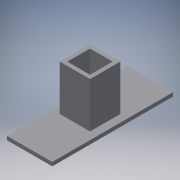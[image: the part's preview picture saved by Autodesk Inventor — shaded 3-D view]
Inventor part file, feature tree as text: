
AUTODESK INVENTOR PART (.ipt)
format: ipt  version: 2016 (Build 200138000, 138)  size: 104,960 bytes
history: native  units: in
note: dims shown in document units (in); Inventor stores cm internally (conversion verified against a paired STEP export)
features: extrude x2, sketch x2
ambient origin geometry x8: Origin, YZ Plane, XZ Plane, XY Plane, X Axis, Y Axis, Z Axis, Center Point
bodies: Solid1 (feature_tree)
feature tree (4):
  extrude  "Extrusion1"  Depth=4.0in
  extrude  "Extrusion3"  Depth=1.0in
  sketch  "Sketch1"  dims[d0=1.5in d1=4.0in]
  sketch  "Sketch3"  dims[d2=0.125in d3=0.0in d8=1.0in d9=1.0in d10=0.25in d11=1.5in d12=0.125in d13=1.5in d14=0.0in]
